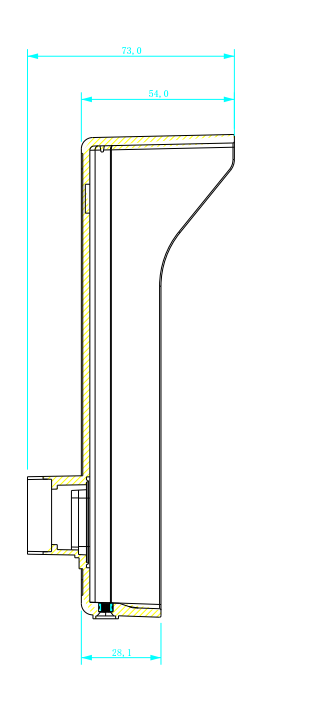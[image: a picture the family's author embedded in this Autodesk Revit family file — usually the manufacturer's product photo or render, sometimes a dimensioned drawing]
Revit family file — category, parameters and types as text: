
# Revit family: AA-07BD
name_source: partatom
category: Устройства связи
units: mm (PartAtom-declared; Revit-internal decimal feet)

## family parameters
Всегда вертикально = Нет
На основе рабочей плоскости = Да
Общий = Да
При загрузке вырезать с полостями = Нет
Размер круглого соединителя = Использовать диаметр
Сохранять ориентацию аннотаций = Нет
Тип детали = Нормальный
Точка расчета площади = Нет

## types (1)
- AA-07BD
    ADSK_URL документации изделия = https://drive.google.com
    ADSK_URL страницы изделия = https://bas-ip.com
    ADSK_Версия Revit = Revit 2020
    ADSK_Единица измерения = шт
    ADSK_Завод-изготовитель = BAS-IP
    ADSK_Классификация нагрузок = Вызывная панель
    ADSK_Количество фаз = 1
    ADSK_Коэффициент мощности = 0.9
    ADSK_Марка = AA-07BD
    ADSK_Наименование = ВЫЗЫВНАЯ ПАНЕЛЬ AA-07BD
    ADSK_Наименование краткое = AA-07BD
    ADSK_Напряжение = 12 В
    ADSK_Номинальная мощность = 7 Вт
    ADSK_Полная мощность = 7 В·А
    ADSK_Размер_Длина = 155 мм
    ADSK_Размер_Толщина = 55 мм
    ADSK_Размер_Ширина = 375 мм
    BIM library = https://bimlib.ru
    IK-код = IK07
    URL = https://www.bas-ip.ru
    Аутентификация = Отдельный пароль для настройки, WEB–интерфейс и RTSP сервис
    Выходное видео = HalfHD (1280×720),H.264 Main Profile
    Группа модели = Вызывная панель
    Дисплей = 4,3” TFT, цветной с подсветкой
    Дополнительно = Поддержка ПО «Link», SIP P2P, Встроенное реле, Открытый API
    Допустимая влажность при хранении = 0% – 60%
    Допустимая влажность при эксплуатации = 0% – 86%
    Изготовитель = BAS-IP
    Изображение типоразмера = <Нет>
    Интеграция со СКУД = Выход WIEGAND-26/32/34/37/40/42/56/58/64
    Интерфейс = Многоязычный графическийи WEB-интерфейс
    Камера = 1/3”
    Класс степени защиты = IP65
    Кнопки быстрого вызова = Кнопка вызова консьержа
    Количество идентификаторов в памяти панели = 20 000
    Контроль доступа = UKEY (EM-Marin/ MIFARE®/NFC/Bluetooth)
    Корпус = Металлический
    Минимальная освещенность = 0,01 LuX
    Ночная подсветка = 6 светодиодов
    Описание = Многоабонентская вызывная панель AA-07BD SILVER – отличное решение для офисных зданий, многоквартирных комплексов и коттеджных поселков. Отличительной особенностью данной панели является цветной TFT экран с подсветкой, а также IP камера высокого разрешения с большими углами обзора. AA-07BD поддерживает мобильный доступ BAS-IP UKEY.
    Открытие замка = С монитора. По пин-коду. По QR-коду. По гостевой ссылке. По карте. Из приложения BAS-IP Intercom. Из приложения BAS-IP UKEY. Из приложения BAS-IP Link. По API
    Отметка по умолчанию = 0 мм
    Питание = +12 В (+8% -6%)
    Потребление питания = 6,5 Вт, в режиме ожидания – 3,5 Вт
    Размер панели = 155х375х55 мм
    Размер под установку = 141х351х60 мм
    Разрешение камеры = 2.0 Мп
    Температурный режим = -40 ... +65 °С
    Тип клавиатуры = Механические кнопки с подсветкой
    Тип панели = Многоквартирная
    Тип установки = Врезная, накладная с BR-AA
    Угол обзора = 110° (по горизонтали)
    Цветовое решение = Silver
